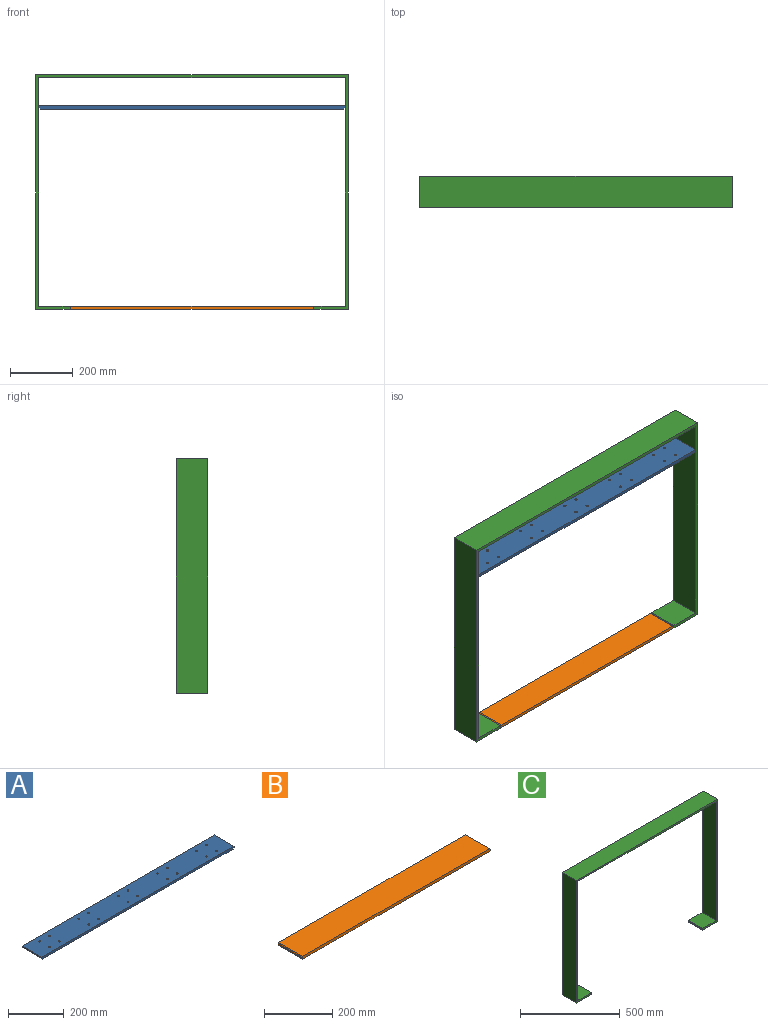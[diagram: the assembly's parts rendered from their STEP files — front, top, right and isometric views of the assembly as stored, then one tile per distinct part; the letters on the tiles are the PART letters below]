
ASSEMBLY  parts=3 mates=2
PART A: 48 faces, bbox 980x100x10 mm
  f0: plane 980x100mm, normal (0,0,1), area 97230.3mm2, adj f1,f3,f4,f5,f6,f8,f10,f12
  f1: plane 100x5mm, normal (-1,0,0), area 500mm2, adj f0,f4,f5,f47
  f2: plane 970x100mm, normal (0,0,-1), area 94162.6mm2, adj f4,f5,f7,f9,f11,f13,f15,f17
  f3: plane 100x5mm, normal (1,0,0), area 500mm2, adj f0,f4,f5,f46
  f4: plane 980x10mm, normal (0,1,0), area 9775mm2, adj f0,f1,f2,f3,f46,f47
  f5: plane 980x10mm, normal (0,-1,0), area 9775mm2, adj f0,f1,f2,f3,f46,f47
  f6: cylinder r=3.5mm len=7mm, axis (0,0,-1), area 149.1mm2, adj f0,f7
  f7: cone r=3.5mm half-angle=45deg, axis (0,0,-1), area 146.2mm2, adj f2,f6
  f8: cylinder r=3.5mm len=7mm, axis (0,0,-1), area 149.1mm2, adj f0,f9
  f9: cone r=3.5mm half-angle=45deg, axis (0,0,-1), area 146.2mm2, adj f2,f8
  f10: cylinder r=3.5mm len=7mm, axis (0,0,-1), area 149.1mm2, adj f0,f11
  f11: cone r=3.5mm half-angle=45deg, axis (0,0,-1), area 146.2mm2, adj f2,f10
  f12: cylinder r=3.5mm len=7mm, axis (0,0,-1), area 149.1mm2, adj f0,f13
  f13: cone r=3.5mm half-angle=45deg, axis (0,0,-1), area 146.2mm2, adj f2,f12
  f14: cylinder r=3.5mm len=7mm, axis (0,0,-1), area 149.1mm2, adj f0,f15
  f15: cone r=3.5mm half-angle=45deg, axis (0,0,-1), area 146.2mm2, adj f2,f14
  f16: cylinder r=3.5mm len=7mm, axis (0,0,-1), area 149.1mm2, adj f0,f17
  f17: cone r=3.5mm half-angle=45deg, axis (0,0,-1), area 146.2mm2, adj f2,f16
  f18: cylinder r=3.5mm len=7mm, axis (0,0,-1), area 149.1mm2, adj f0,f19
  f19: cone r=3.5mm half-angle=45deg, axis (0,0,-1), area 146.2mm2, adj f2,f18
  f20: cylinder r=3.5mm len=7mm, axis (0,0,-1), area 149.1mm2, adj f0,f21
  f21: cone r=3.5mm half-angle=45deg, axis (0,0,-1), area 146.2mm2, adj f2,f20
  f22: cylinder r=3.5mm len=7mm, axis (0,0,-1), area 149.1mm2, adj f0,f23
  f23: cone r=3.5mm half-angle=45deg, axis (0,0,-1), area 146.2mm2, adj f2,f22
  f24: cylinder r=3.5mm len=7mm, axis (0,0,-1), area 149.1mm2, adj f0,f25
  f25: cone r=3.5mm half-angle=45deg, axis (0,0,-1), area 146.2mm2, adj f2,f24
  f26: cylinder r=3.5mm len=7mm, axis (0,0,-1), area 149.1mm2, adj f0,f27
  f27: cone r=3.5mm half-angle=45deg, axis (0,0,-1), area 146.2mm2, adj f2,f26
  f28: cylinder r=3.5mm len=7mm, axis (0,0,-1), area 149.1mm2, adj f0,f29
  f29: cone r=3.5mm half-angle=45deg, axis (0,0,-1), area 146.2mm2, adj f2,f28
  f30: cylinder r=3.5mm len=7mm, axis (0,0,-1), area 149.1mm2, adj f0,f31
  f31: cone r=3.5mm half-angle=45deg, axis (0,0,-1), area 146.2mm2, adj f2,f30
  f32: cylinder r=3.5mm len=7mm, axis (0,0,-1), area 149.1mm2, adj f0,f33
  f33: cone r=3.5mm half-angle=45deg, axis (0,0,-1), area 146.2mm2, adj f2,f32
  f34: cylinder r=3.5mm len=7mm, axis (0,0,-1), area 149.1mm2, adj f0,f35
  f35: cone r=3.5mm half-angle=45deg, axis (0,0,-1), area 146.2mm2, adj f2,f34
  f36: cylinder r=3.5mm len=7mm, axis (0,0,-1), area 149.1mm2, adj f0,f37
  f37: cone r=3.5mm half-angle=45deg, axis (0,0,-1), area 146.2mm2, adj f2,f36
  f38: cylinder r=3.5mm len=7mm, axis (0,0,-1), area 149.1mm2, adj f0,f39
  f39: cone r=3.5mm half-angle=45deg, axis (0,0,-1), area 146.2mm2, adj f2,f38
  f40: cylinder r=3.5mm len=7mm, axis (0,0,-1), area 149.1mm2, adj f0,f41
  f41: cone r=3.5mm half-angle=45deg, axis (0,0,-1), area 146.2mm2, adj f2,f40
  f42: cylinder r=3.5mm len=7mm, axis (0,0,-1), area 149.1mm2, adj f0,f43
  f43: cone r=3.5mm half-angle=45deg, axis (0,0,-1), area 146.2mm2, adj f2,f42
  f44: cylinder r=3.5mm len=7mm, axis (0,0,-1), area 149.1mm2, adj f0,f45
  f45: cone r=3.5mm half-angle=45deg, axis (0,0,-1), area 146.2mm2, adj f2,f44
  f46: plane 100x5mm, normal (0.71,0,-0.71), area 707.1mm2, adj f2,f3,f4,f5
  f47: plane 100x5mm, normal (-0.71,0,-0.71), area 707.1mm2, adj f1,f2,f4,f5
PART B: 10 faces, bbox 780x100x10 mm
  f0: plane 774x100mm, normal (0,0,1), area 77400mm2, adj f4,f5,f6,f9
  f1: plane 100x4mm, normal (-1,0,0), area 400mm2, adj f4,f5,f6,f7
  f2: plane 774x100mm, normal (0,0,-1), area 77400mm2, adj f4,f5,f7,f8
  f3: plane 100x4mm, normal (1,0,0), area 400mm2, adj f4,f5,f8,f9
  f4: plane 780x10mm, normal (0,1,0), area 7782mm2, adj f0,f1,f2,f3,f6,f7,f8,f9
  f5: plane 780x10mm, normal (0,-1,0), area 7782mm2, adj f0,f1,f2,f3,f6,f7,f8,f9
  f6: plane 100x3mm, normal (-0.71,0,0.71), area 424.3mm2, adj f0,f1,f4,f5
  f7: plane 100x3mm, normal (-0.71,0,-0.71), area 424.3mm2, adj f1,f2,f4,f5
  f8: plane 100x3mm, normal (0.71,0,-0.71), area 424.3mm2, adj f2,f3,f4,f5
  f9: plane 100x3mm, normal (0.71,0,0.71), area 424.3mm2, adj f0,f3,f4,f5
PART C: 18 faces, bbox 1000x100x750 mm
  f0: plane 100x97mm, normal (0,0,1), area 9700mm2, adj f2,f9,f11,f17
  f1: plane 100x97mm, normal (0,0,1), area 9700mm2, adj f2,f8,f11,f15
  f2: plane 1000x750mm, normal (0,-1,0), area 26782mm2, adj f0,f1,f3,f4,f5,f6,f7,f8
  f3: plane 107x100mm, normal (0,0,-1), area 10700mm2, adj f2,f5,f11,f16
  f4: plane 1000x100mm, normal (0,0,1), area 100000mm2, adj f2,f5,f10,f11
  f5: plane 750x100mm, normal (-1,0,0), area 75000mm2, adj f2,f3,f4,f11
  f6: plane 107x100mm, normal (0,0,-1), area 10700mm2, adj f2,f10,f11,f14
  f7: plane 980x100mm, normal (0,0,-1), area 98000mm2, adj f2,f8,f9,f11
  f8: plane 730x100mm, normal (-1,0,0), area 73000mm2, adj f1,f2,f7,f11
  f9: plane 730x100mm, normal (1,0,0), area 73000mm2, adj f0,f2,f7,f11
  f10: plane 750x100mm, normal (1,0,0), area 75000mm2, adj f2,f4,f6,f11
  f11: plane 1000x750mm, normal (0,1,0), area 26782mm2, adj f0,f1,f3,f4,f5,f6,f7,f8
  f12: plane 100x4mm, normal (-1,0,0), area 400mm2, adj f2,f11,f14,f15
  f13: plane 100x4mm, normal (1,0,0), area 400mm2, adj f2,f11,f16,f17
  f14: plane 100x3mm, normal (-0.71,0,-0.71), area 424.3mm2, adj f2,f6,f11,f12
  f15: plane 100x3mm, normal (-0.71,0,0.71), area 424.3mm2, adj f1,f2,f11,f12
  f16: plane 100x3mm, normal (0.71,0,-0.71), area 424.3mm2, adj f2,f3,f11,f13
  f17: plane 100x3mm, normal (0.71,0,0.71), area 424.3mm2, adj f0,f2,f11,f13
PLACE A t=(-89.81,-37.43,-173.36)mm
PLACE B t=(-89.81,-37.43,-172.36)mm
PLACE C t=(-89.81,-37.43,-173.36)mm
MATE fastened B.f5 <-> C.f2  axis (0,-1,0) through (-479.81,-37.43,-541.36)mm
MATE planar C.f2 <-> A.f5  axis (0,-1,0) through (-579.81,-37.43,191.64)mm
